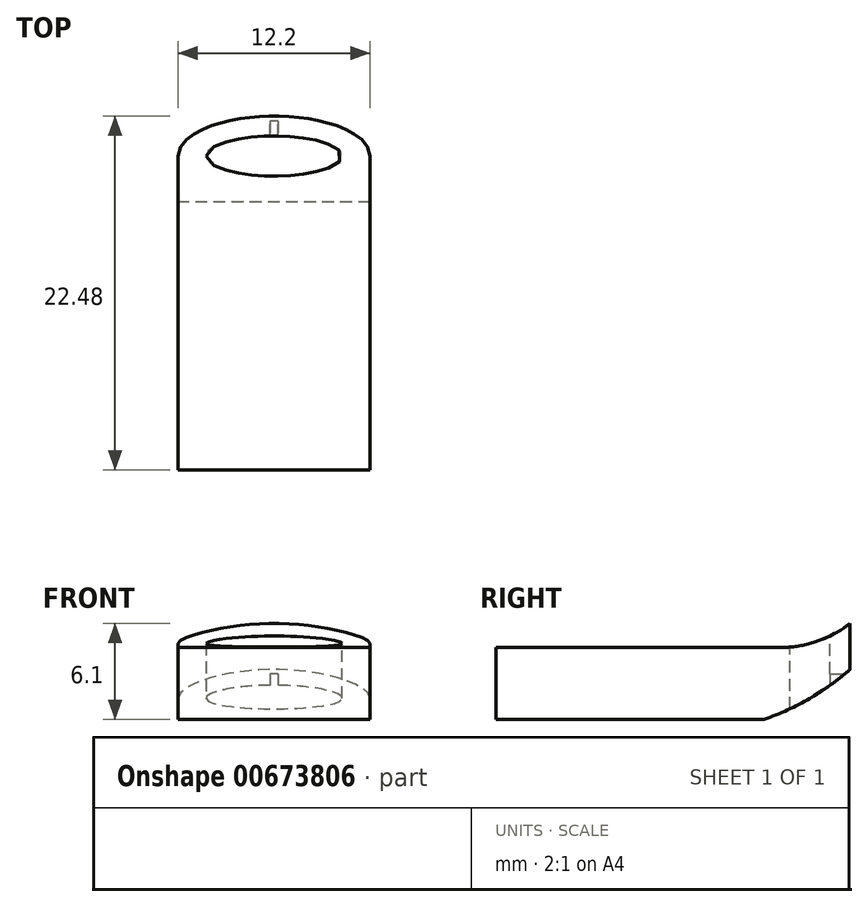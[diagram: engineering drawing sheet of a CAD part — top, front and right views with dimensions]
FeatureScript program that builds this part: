
annotation { "Feature Type Name" : "Feature", "Feature Type Description" : "" }
export const myFeature = defineFeature(function(context is Context, id is Id, definition is map)
    precondition{}
    {
        {
            var Q0;
            Q0=qCreatedBy(makeId("Top.planeOp"),FACE);
            var sketch = newSketch(context, id + "F0", { "sketchPlane" : qUnion([Q0])});
            skLineSegment(sketch, "E0", {"start": v(-6.1, 0) * mm, "end": v(-6.1, 19.94) * mm});
            skEllipse(sketch, "E1", {"center": v(0, 19.94) * mm, "majorRadius": 4.32 * mm, "minorRadius": 1.27 * mm, "majorAxis": v(-1, 0)});
            skEllipticalArc(sketch, "E2", {});
            skLineSegment(sketch, "E3", {"start": v(0, 0) * mm, "end": v(0, 22.48) * mm, "construction": true});
            skLineSegment(sketch, "E4", {"start": v(-6.1, 0) * mm, "end": v(6.1, 0) * mm});
            skLineSegment(sketch, "E5", {"start": v(6.1, 0) * mm, "end": v(6.1, 19.94) * mm});
            const initialGuessF0  = {"E2": [0, 0.019939, -1, 0, 0.006096, 0.00254, 3.141592653589793, 0]};
            skSetInitialGuess(sketch, initialGuessF0);
            skSolve(sketch);
        }
        {
            var Q0;
            Q0 = qSketchRegion(id + "F0", true);
            extrude(context, id + "F1", {"entities" : qUnion([Q0]), "depth" : 6.1 * mm, "offsetDistance" : 25.4 * mm});
        }
        {
            var Q0;
            Q0=qCreatedBy(makeId("Right.planeOp"),FACE);
            var sketch = newSketch(context, id + "F2", { "sketchPlane" : qUnion([Q0])});
            skLineSegment(sketch, "E6", {"start": v(0, 0) * mm, "end": v(17.02, 0) * mm});
            skLineSegment(sketch, "E7", {"start": v(0, 0) * mm, "end": v(0, 4.57) * mm});
            skLineSegment(sketch, "E8", {"start": v(0, 4.57) * mm, "end": v(18.03, 4.57) * mm});
            skArc(sketch, "E9", {"start": v(18.03, 4.57) * mm, "mid": v(20.38, 4.96) * mm, "end": v(22.48, 6.1) * mm});
            skPoint(sketch, "E10", {"position": v(21.2, 2.9) * mm});
            skLineSegment(sketch, "E11", {"start": v(22.48, 7.11) * mm, "end": v(22.48, 0) * mm, "construction": true});
            skLineSegment(sketch, "E12", {"start": v(21.2, 6.1) * mm, "end": v(21.2, 0) * mm, "construction": true});
            skPoint(sketch, "E13", {"position": v(22.48, 3.18) * mm});
            skLineSegment(sketch, "E14.0", {"start": v(19.94, 6.1) * mm, "end": v(22.48, 6.1) * mm, "construction": true});
            skArc(sketch, "E15", {"start": v(17.02, 0) * mm, "mid": v(19.9, 1.33) * mm, "end": v(22.48, 3.18) * mm});
            skLineSegment(sketch, "E16", {"start": v(22.48, 3.18) * mm, "end": v(22.48, 6.1) * mm});
            skSolve(sketch);
        }
        {
            var Q0;
            Q0 = qSketchRegion(id + "F2", true);
            extrude(context, id + "F3", {"entities" : qUnion([Q0]), "operationType" : NewBodyOperationType.INTERSECT, "endBound" : BoundingType.THROUGH_ALL, "depth" : 25.4 * mm, "offsetDistance" : 25.4 * mm, "hasSecondDirection" : true, "secondDirectionBound" : SecondDirectionBoundingType.THROUGH_ALL, "secondDirectionOppositeDirection" : true, "secondDirectionDepth" : 25.4 * mm});
        }
        {
            var Q0;
            Q0=makeQuery(id+"F1.opExtrude","CAP_FACE",FACE,{"disambiguationData":[OSD([sQuery(id+"F0.wireOp",EDGE,"E0"),sQuery(id+"F0.wireOp",EDGE,"E1"),sQuery(id+"F0.wireOp",EDGE,"E2"),sQuery(id+"F0.wireOp",EDGE,"E4"),sQuery(id+"F0.wireOp",EDGE,"E5")])],"isStart":true});
            var sketch = newSketch(context, id + "F4", { "sketchPlane" : qUnion([Q0])});
            skLineSegment(sketch, "E17.bottom", {"start": v(-0.25, -20.83) * mm, "end": v(0.25, -20.83) * mm});
            skLineSegment(sketch, "E17.top", {"start": v(-0.25, -22.73) * mm, "end": v(0.25, -22.73) * mm});
            skLineSegment(sketch, "E17.left", {"start": v(-0.25, -20.83) * mm, "end": v(-0.25, -22.73) * mm});
            skLineSegment(sketch, "E17.right", {"start": v(0.25, -20.83) * mm, "end": v(0.25, -22.73) * mm});
            skLineSegment(sketch, "E18", {"start": v(0, 0) * mm, "end": v(0, -20.83) * mm, "construction": true});
            skSolve(sketch);
        }
        {
            var Q0;
            Q0=makeQuery(id+"F4.imprint","IMPRINT",FACE,{"disambiguationData":[TD([[makeQuery(id+"F4.imprint","IMPRINT",EDGE,{"derivedFrom":sQuery(id+"F4.wireOp",EDGE,"E17.bottom")}),-1.0]])]});
            extrude(context, id + "F5", {"entities" : qUnion([Q0]), "operationType" : NewBodyOperationType.REMOVE, "oppositeDirection" : true, "depth" : 2.9 * mm, "offsetDistance" : 25.4 * mm});
        }
    });
